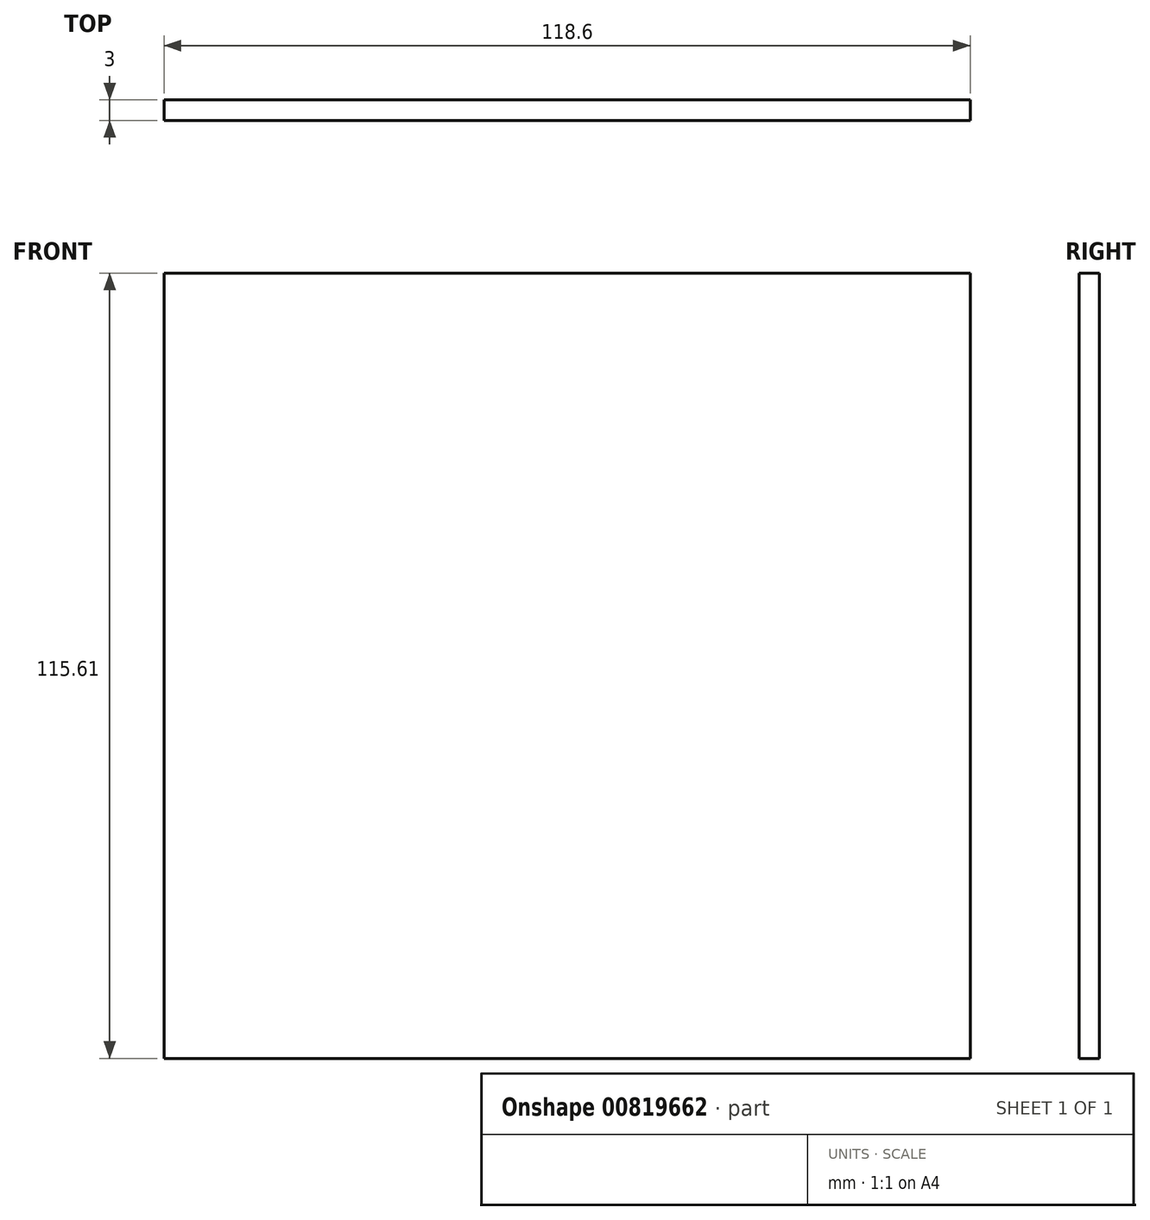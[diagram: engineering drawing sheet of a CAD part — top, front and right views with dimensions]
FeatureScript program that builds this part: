
annotation { "Feature Type Name" : "Feature", "Feature Type Description" : "" }
export const myFeature = defineFeature(function(context is Context, id is Id, definition is map)
    precondition{}
    {
        {
            var Q0;
            Q0=qCreatedBy(makeId("Front.planeOp"),FACE);
            var sketch = newSketch(context, id + "F0", { "sketchPlane" : qUnion([Q0])});
            skLineSegment(sketch, "E0.bottom", {"start": v(0, 0) * mm, "end": v(118.6, 0) * mm});
            skLineSegment(sketch, "E0.top", {"start": v(0, 115.61) * mm, "end": v(118.6, 115.61) * mm});
            skLineSegment(sketch, "E0.left", {"start": v(0, 0) * mm, "end": v(0, 115.61) * mm});
            skLineSegment(sketch, "E0.right", {"start": v(118.6, 0) * mm, "end": v(118.6, 115.61) * mm});
            skSolve(sketch);
        }
        {
            var Q0;
            Q0=makeQuery(id+"F0.imprint","IMPRINT",FACE,{"disambiguationData":[TD([[makeQuery(id+"F0.imprint","IMPRINT",EDGE,{"derivedFrom":sQuery(id+"F0.wireOp",EDGE,"E0.bottom")}),1.0]])]});
            extrude(context, id + "F1", {"entities" : qUnion([Q0]), "depth" : 3 * mm, "offsetDistance" : 25 * mm});
        }
    });
